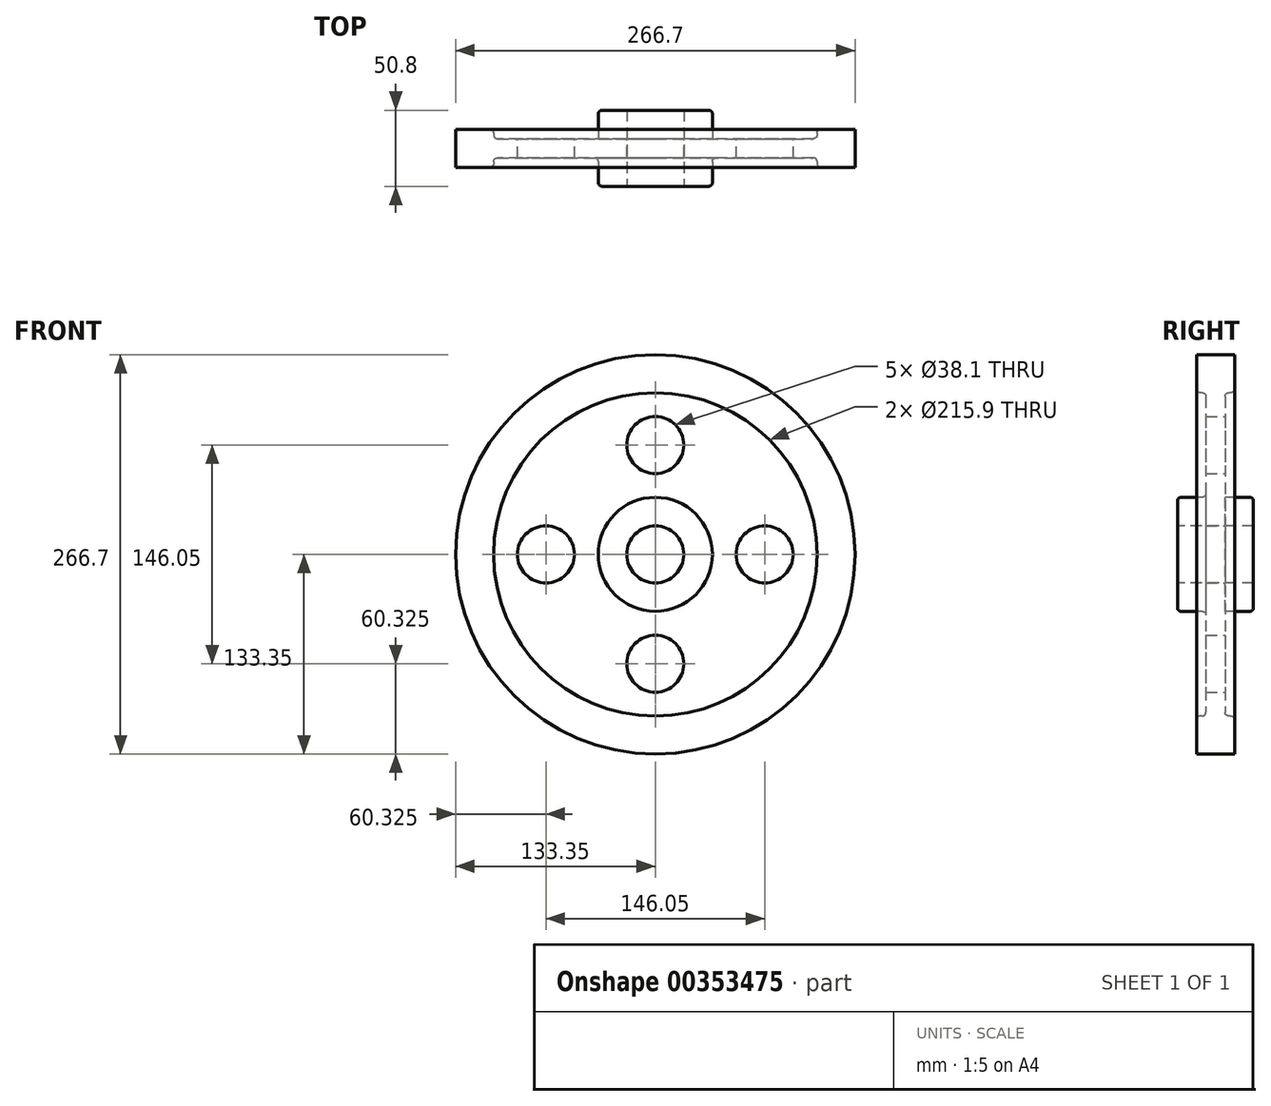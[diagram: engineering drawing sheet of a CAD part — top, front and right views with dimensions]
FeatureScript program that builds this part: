
annotation { "Feature Type Name" : "Feature", "Feature Type Description" : "" }
export const myFeature = defineFeature(function(context is Context, id is Id, definition is map)
    precondition{}
    {
        {
            var Q0;
            Q0=qCreatedBy(makeId("Right.planeOp"),FACE);
            var sketch = newSketch(context, id + "F0", { "sketchPlane" : qUnion([Q0])});
            skLineSegment(sketch, "E0", {"start": v(0, 0) * mm, "end": v(84.94, 0) * mm, "construction": true});
            skLineSegment(sketch, "E1.0", {"start": v(0, 19.05) * mm, "end": v(25.4, 19.05) * mm});
            skLineSegment(sketch, "E2.0", {"start": v(6.35, 38.1) * mm, "end": v(25.4, 38.1) * mm});
            skLineSegment(sketch, "E3.0", {"start": v(6.35, 107.95) * mm, "end": v(12.7, 107.95) * mm});
            skLineSegment(sketch, "E4.0", {"start": v(0, 133.35) * mm, "end": v(12.7, 133.35) * mm});
            skLineSegment(sketch, "E5", {"start": v(0, 133.35) * mm, "end": v(0, 0) * mm, "construction": true});
            skLineSegment(sketch, "E6.0", {"start": v(25.4, 38.1) * mm, "end": v(25.4, 19.05) * mm});
            skLineSegment(sketch, "E7.0", {"start": v(6.35, 107.95) * mm, "end": v(6.35, 38.1) * mm});
            skLineSegment(sketch, "E8.0", {"start": v(12.7, 133.35) * mm, "end": v(12.7, 107.95) * mm});
            skLineSegment(sketch, "E9.MirrorCS", {"start": v(0, 19.05) * mm, "end": v(-25.4, 19.05) * mm});
            skLineSegment(sketch, "E10.MirrorCS", {"start": v(-25.4, 38.1) * mm, "end": v(-25.4, 19.05) * mm});
            skLineSegment(sketch, "E11.MirrorCS", {"start": v(-6.35, 38.1) * mm, "end": v(-25.4, 38.1) * mm});
            skLineSegment(sketch, "E12.MirrorCS", {"start": v(-6.35, 107.95) * mm, "end": v(-6.35, 38.1) * mm});
            skLineSegment(sketch, "E13.MirrorCS", {"start": v(-6.35, 107.95) * mm, "end": v(-12.7, 107.95) * mm});
            skLineSegment(sketch, "E14.MirrorCS", {"start": v(-12.7, 133.35) * mm, "end": v(-12.7, 107.95) * mm});
            skLineSegment(sketch, "E15.MirrorCS", {"start": v(0, 133.35) * mm, "end": v(-12.7, 133.35) * mm});
            skSolve(sketch);
        }
        {
            var Q0;
            Q0=makeQuery(id+"F0.imprint","IMPRINT",FACE,{"disambiguationData":[TD([[makeQuery(id+"F0.imprint","IMPRINT",EDGE,{"derivedFrom":sQuery(id+"F0.wireOp",EDGE,"E1.0")}),1.0]])]});
            var Q1;
            Q1=sQuery(id+"F0.wireOp",EDGE,"E0");
            revolve(context, id + "F1", {"entities" : qUnion([Q0]), "axis" : qUnion([Q1]), "revolveType" : RevolveType.FULL});
        }
        {
            var Q0;
            Q0=makeQuery(id+"F1.opRevolve","SWEPT_FACE",FACE,{"disambiguationData":[OSD([sQuery(id+"F0.wireOp",EDGE,"E7.0")])]});
            var sketch = newSketch(context, id + "F2", { "sketchPlane" : qUnion([Q0])});
            skLineSegment(sketch, "E16", {"start": v(0, 0) * mm, "end": v(0, 73.03) * mm});
            skCircle(sketch, "E17", {"center": v(0, 73.03) * mm, "radius": 19.05 * mm});
            skCircle(sketch, "E18.1.0", {"center": v(-73.03, 0) * mm, "radius": 19.05 * mm});
            skCircle(sketch, "E18.2.0", {"center": v(0, -73.03) * mm, "radius": 19.05 * mm});
            skCircle(sketch, "E18.3.0", {"center": v(73.03, 0) * mm, "radius": 19.05 * mm});
            skPoint(sketch, "E18.center", {"position": v(0, 0) * mm});
            skSolve(sketch);
        }
        {
            var Q0;
            Q0=makeQuery(id+"F2.imprint","IMPRINT",FACE,{"disambiguationData":[TD([[makeQuery(id+"F2.imprint","IMPRINT",EDGE,{"derivedFrom":sQuery(id+"F2.wireOp",EDGE,"E18.3.0")}),1.0]])]});
            var Q1;
            Q1=makeQuery(id+"F2.imprint","IMPRINT",FACE,{"disambiguationData":[TD([[makeQuery(id+"F2.imprint","IMPRINT",EDGE,{"derivedFrom":sQuery(id+"F2.wireOp",EDGE,"E18.1.0")}),1.0]])]});
            var Q2;
            Q2=makeQuery(id+"F2.imprint","IMPRINT",FACE,{"disambiguationData":[TD([[makeQuery(id+"F2.imprint","IMPRINT",EDGE,{"derivedFrom":sQuery(id+"F2.wireOp",EDGE,"E17")}),1.0]])]});
            var Q3;
            Q3=makeQuery(id+"F2.imprint","IMPRINT",FACE,{"disambiguationData":[TD([[makeQuery(id+"F2.imprint","IMPRINT",EDGE,{"derivedFrom":sQuery(id+"F2.wireOp",EDGE,"E18.2.0")}),1.0]])]});
            extrude(context, id + "F3", {"entities" : qUnion([Q0, Q1, Q2, Q3]), "operationType" : NewBodyOperationType.REMOVE, "oppositeDirection" : true, "depth" : 25.4 * mm});
        }
        {
            var Q0;
            Q0=makeQuery(id+"F1.opRevolve","SWEPT_EDGE",EDGE,{"disambiguationData":[OSD([sQuery(id+"F0.wireOp",EDGE,"E12.MirrorCS"),sQuery(id+"F0.wireOp",EDGE,"E13.MirrorCS")])]});
            var Q1;
            Q1=makeQuery(id+"F1.opRevolve","SWEPT_EDGE",EDGE,{"disambiguationData":[OSD([sQuery(id+"F0.wireOp",EDGE,"E13.MirrorCS"),sQuery(id+"F0.wireOp",EDGE,"E14.MirrorCS")])]});
            var Q2;
            Q2=makeQuery(id+"F1.opRevolve","SWEPT_EDGE",EDGE,{"disambiguationData":[OSD([sQuery(id+"F0.wireOp",EDGE,"E10.MirrorCS"),sQuery(id+"F0.wireOp",EDGE,"E11.MirrorCS")])]});
            var Q3;
            Q3=makeQuery(id+"F1.opRevolve","SWEPT_EDGE",EDGE,{"disambiguationData":[OSD([sQuery(id+"F0.wireOp",EDGE,"E11.MirrorCS"),sQuery(id+"F0.wireOp",EDGE,"E12.MirrorCS")])]});
            fillet(context, id + "F4", {"entities" : qUnion([Q0, Q1, Q2, Q3]), "radius" : 2.54 * mm, "tangentPropagation" : true, "allowEdgeOverflow" : false});
        }
        {
            var Q0;
            Q0=makeQuery(id+"F1.opRevolve","SWEPT_EDGE",EDGE,{"disambiguationData":[OSD([sQuery(id+"F0.wireOp",EDGE,"E2.0"),sQuery(id+"F0.wireOp",EDGE,"E6.0")])]});
            var Q1;
            Q1=makeQuery(id+"F1.opRevolve","SWEPT_EDGE",EDGE,{"disambiguationData":[OSD([sQuery(id+"F0.wireOp",EDGE,"E3.0"),sQuery(id+"F0.wireOp",EDGE,"E8.0")])]});
            var Q2;
            Q2=makeQuery(id+"F1.opRevolve","SWEPT_EDGE",EDGE,{"disambiguationData":[OSD([sQuery(id+"F0.wireOp",EDGE,"E3.0"),sQuery(id+"F0.wireOp",EDGE,"E7.0")])]});
            fillet(context, id + "F5", {"entities" : qUnion([Q0, Q1, Q2]), "radius" : 2.54 * mm, "tangentPropagation" : true, "allowEdgeOverflow" : false});
        }
    });
